# Revit family: NXBTC
name_source: partatom
category: Communication Devices
units: mm (PartAtom-declared; Revit-internal decimal feet)

## family parameters
Cut with Voids When Loaded = No
Host = Face
Maintain Annotation Orientation = No
OmniClass Number = 23.85.80.11.27
OmniClass Title = Lighting Controls
Part Type = Normal
Room Calculation Point = No
Round Connector Dimension = Use Diameter
Shared = Yes

## types (1)
- NXBTC
    Assembly Code = D5090
    Cable = Paint -  Carbon Black
    Default Elevation = 48 "
    Description = The NXBTC Bluetooth® Radio Bridge provides a wireless communication bridge for communication via iOS® or Android™ smart device Apps. The compact bridge connects to and is powered by an NX SmartPORT™. The NXBTC uses Bluetooth technology allowing the radio to easily pair with the smart phone. Communication with the NX system for setup and control requires installation of the NX iOS or Android App on the smart device. The NXBTC version of the Bluetooth Radio Bridge contains a Real Time Clock chip and allows schedules to be downloaded and run in stand-alone NXRC Room Controller applications without a network. The NXBTC version also provides password protection for user access preventing unauthorized Bluetooth connection of a smart device.
    Features = Bluetooth Technology (Version 4.1)
• Easily pairs with smart phone with active Bluetooth radio
• control App available for free download from Apple®
and Google Play™
• Simple RJ45 plug in connection to NX SmartPORT™
• Low voltage device: 24 VDC
• NXBTC provides real time clock function for scheduling
• NXBTC is cULus listed for use in a return air plenum
    Housing Material = Metal-Aluminum Anodized Blue
    Manufacturer = NX Lighting Controls
    Model = NXBTC
    Plug = Glass -  White
    Type Comments = Bluetooth® Radio Controller
    URL = https://www.currentlighting.com
    Voltage = 24V
    Warranty = 5-Years Warranty

## geometry (parser evidence)
native form markers: Sweep x2
no freeform markers — native parametric forms only
